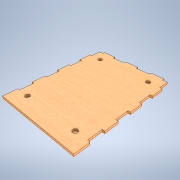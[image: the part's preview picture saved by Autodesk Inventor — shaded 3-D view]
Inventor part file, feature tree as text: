
AUTODESK INVENTOR PART (.ipt)
format: ipt  version: 2021 (Build 250183000, 183)  size: 221,184 bytes
history: native  units: mm
features: extrude x3, sketch x2, other x1
ambient origin geometry x8: Origin, YZ Plane, XZ Plane, XY Plane, X Axis, Y Axis, Z Axis, Center Point
bodies: Body1 (feature_tree)
feature tree (6):
  other  "DoosjeOnderkant"
  extrude  "Extrusion2"  Depth=140.0mm
  extrude  "Extrusion3"  Depth=3.0mm TaperAngle=0.0deg
  extrude  "Extrusion4"  Depth=2.5mm TaperAngle=0.0deg
  sketch  "Sketch3"  dims[d4=105.0mm d5=140.0mm]
  sketch  "Sketch5"  dims[d6=3.0mm d7=0.0mm d29=3.0mm d30=0.0mm d41=2.5mm d42=0.0mm d51=3.0mm d52=17.5mm d53=17.5mm d54=17.5mm d55=17.5mm d56=17.5mm d58=3.0mm d65=17.5mm d66=17.5mm d67=17.5mm d69=5.75mm d70=5.75mm d71=17.5mm d72=17.5mm d73=20.0mm d75=50.5mm d76=20.0mm d78=68.0mm d81=6.0mm d84=27.25mm d85=36.0mm d2=0.5mm d3=0.872665mm]
